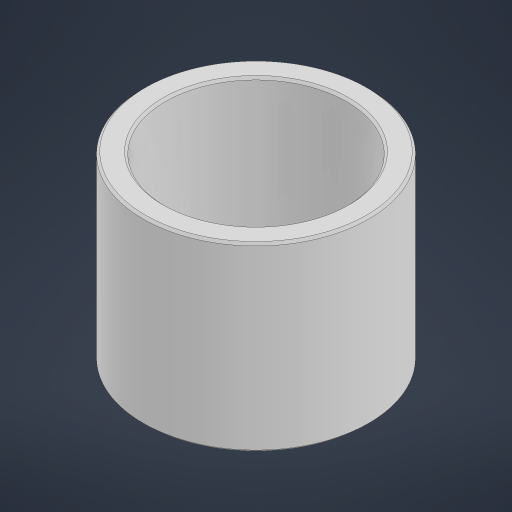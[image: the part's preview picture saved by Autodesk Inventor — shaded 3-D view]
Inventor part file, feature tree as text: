
AUTODESK INVENTOR PART (.ipt)
format: ipt  version: 2023 (Build 270158000, 158)  size: 171,008 bytes
history: native  units: in
note: dims shown in document units (in); Inventor stores cm internally (conversion verified against a paired STEP export)
features: chamfer x1
ambient origin geometry x8: Origin, YZ Plane, XZ Plane, XY Plane, X Axis, Y Axis, Z Axis, Center Point
bodies: Solid1 (feature_tree)
feature tree (1):
  chamfer  "Chamfer1"  [1 undecoded]
note: 1 required parameter value undecoded (feature->parameter linkage not recoverable at this tier; creation-order binding heuristic only, values carry confidence <= 0.55)
